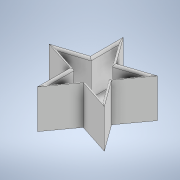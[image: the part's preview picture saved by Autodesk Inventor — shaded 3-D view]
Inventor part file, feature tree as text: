
AUTODESK INVENTOR PART (.ipt)
format: ipt  version: 2020.3 (Build 243373000, 373)  size: 162,816 bytes
history: native  units: mm
features: extrude x4, sketch x4, fillet x1
ambient origin geometry x8: Origin, YZ Plane, XZ Plane, XY Plane, X Axis, Y Axis, Z Axis, Center Point
bodies: Solid1 (feature_tree)
feature tree (9):
  extrude  "Extrusion1"  Depth=5.0mm
  extrude  "Extrusion2"  Depth=5.0mm
  extrude  "Extrusion3"  Depth=2.5mm
  extrude  "Extrusion4"  Depth=40.0mm TaperAngle=0.0deg
  fillet  "Fillet1"  Radius=2.5mm
  sketch  "Sketch1"  dims[d1=5.0mm d2=0.0mm d3=8.5mm]
  sketch  "Sketch2"  dims[d4=2.0mm d5=0.0mm d6=5.0mm]
  sketch  "Sketch3"  dims[d7=2.0mm d8=0.0mm d10=2.5mm]
  sketch  "Sketch4"  dims[d11=8.1mm d12=40.0mm d13=0.0mm d14=2.5mm]
